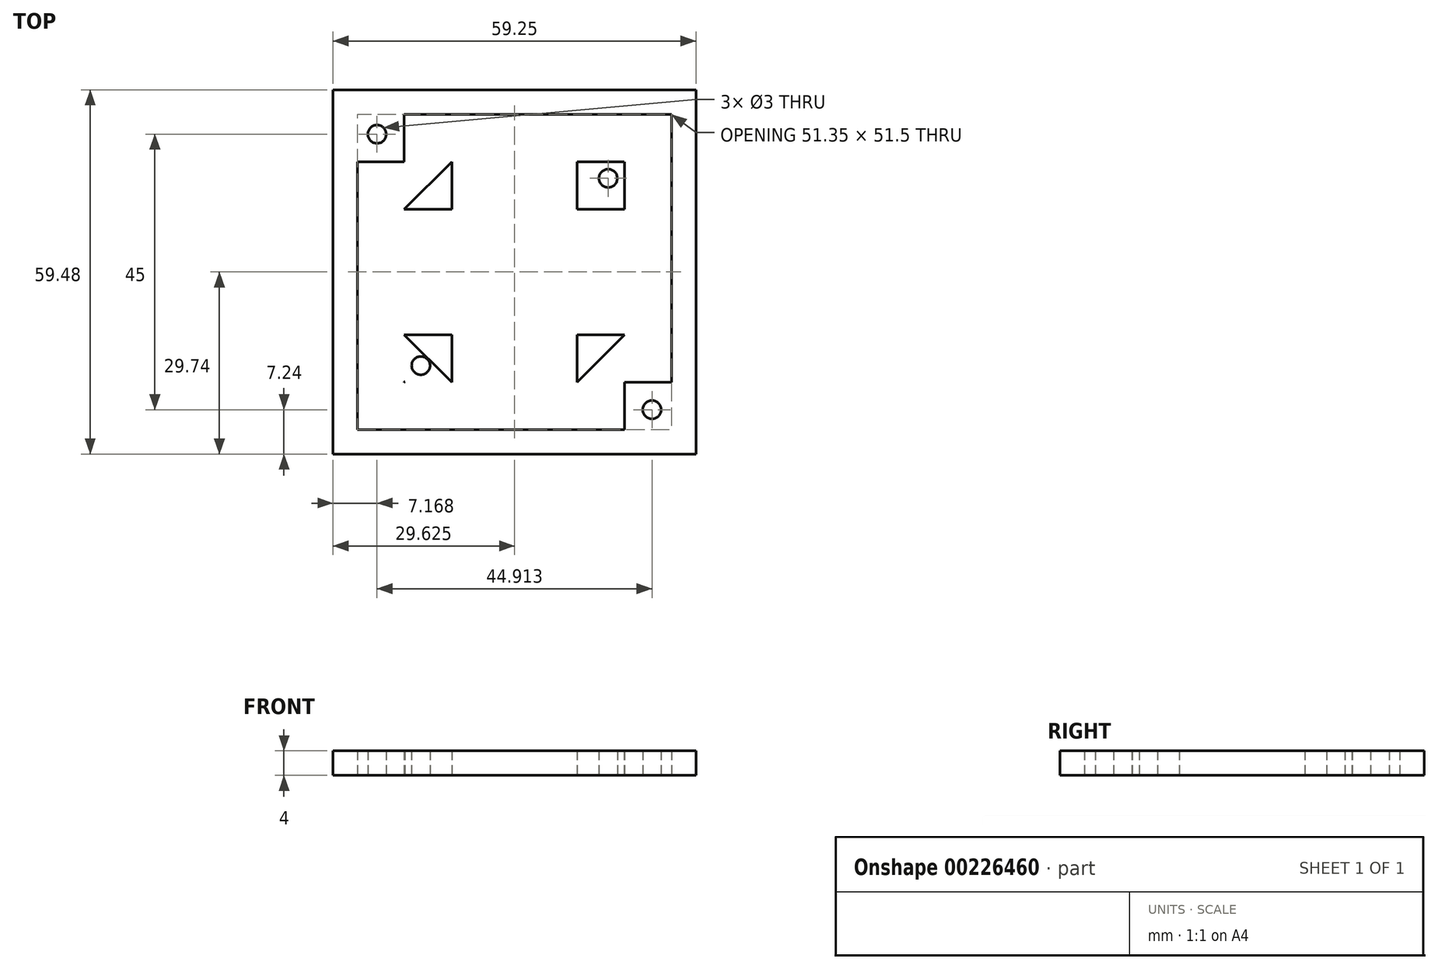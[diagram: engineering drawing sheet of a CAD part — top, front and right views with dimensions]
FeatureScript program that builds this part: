
annotation { "Feature Type Name" : "Feature", "Feature Type Description" : "" }
export const myFeature = defineFeature(function(context is Context, id is Id, definition is map)
    precondition{}
    {
        {
            var Q0;
            Q0=qCreatedBy(makeId("Top.planeOp"),FACE);
            var sketch = newSketch(context, id + "F0", { "sketchPlane" : qUnion([Q0])});
            skLineSegment(sketch, "E0.bottom", {"start": v(0, -51.5) * mm, "end": v(51.35, -51.5) * mm});
            skLineSegment(sketch, "E0.top", {"start": v(0, 0) * mm, "end": v(51.35, 0) * mm});
            skLineSegment(sketch, "E0.left", {"start": v(0, -51.5) * mm, "end": v(0, 0) * mm});
            skLineSegment(sketch, "E0.right", {"start": v(51.35, -51.5) * mm, "end": v(51.35, 0) * mm});
            skLineSegment(sketch, "E1.bottom", {"start": v(7.68, -43.75) * mm, "end": v(43.68, -43.75) * mm});
            skLineSegment(sketch, "E1.top", {"start": v(7.68, -7.75) * mm, "end": v(43.68, -7.75) * mm});
            skLineSegment(sketch, "E1.left", {"start": v(7.67, -43.75) * mm, "end": v(7.67, -7.75) * mm});
            skLineSegment(sketch, "E1.right", {"start": v(43.68, -43.75) * mm, "end": v(43.68, -7.75) * mm});
            skLineSegment(sketch, "E2", {"start": v(7.67, -7.75) * mm, "end": v(0, 0) * mm});
            skLineSegment(sketch, "E3", {"start": v(43.68, -7.75) * mm, "end": v(51.35, 0) * mm});
            skLineSegment(sketch, "E4", {"start": v(43.68, -43.75) * mm, "end": v(51.35, -51.5) * mm});
            skLineSegment(sketch, "E5", {"start": v(7.67, -43.75) * mm, "end": v(0, -51.5) * mm});
            skLineSegment(sketch, "E6.bottom", {"start": v(7.67, -7.75) * mm, "end": v(15.42, -7.75) * mm});
            skLineSegment(sketch, "E6.top", {"start": v(7.68, -15.5) * mm, "end": v(15.42, -15.5) * mm});
            skLineSegment(sketch, "E6.left", {"start": v(7.67, -7.75) * mm, "end": v(7.67, -15.5) * mm});
            skLineSegment(sketch, "E6.right", {"start": v(15.42, -7.75) * mm, "end": v(15.42, -15.5) * mm});
            skLineSegment(sketch, "E7.bottom", {"start": v(43.68, -7.75) * mm, "end": v(35.93, -7.75) * mm});
            skLineSegment(sketch, "E7.top", {"start": v(43.68, -15.5) * mm, "end": v(35.93, -15.5) * mm});
            skLineSegment(sketch, "E7.left", {"start": v(43.68, -7.75) * mm, "end": v(43.68, -15.5) * mm});
            skLineSegment(sketch, "E7.right", {"start": v(35.93, -7.75) * mm, "end": v(35.93, -15.5) * mm});
            skLineSegment(sketch, "E8.bottom", {"start": v(43.68, -43.75) * mm, "end": v(35.93, -43.75) * mm});
            skLineSegment(sketch, "E8.top", {"start": v(43.68, -36) * mm, "end": v(35.93, -36) * mm});
            skLineSegment(sketch, "E8.left", {"start": v(43.68, -43.75) * mm, "end": v(43.68, -36) * mm});
            skLineSegment(sketch, "E8.right", {"start": v(35.93, -43.75) * mm, "end": v(35.93, -36) * mm});
            skLineSegment(sketch, "E9.bottom", {"start": v(7.67, -43.75) * mm, "end": v(15.42, -43.75) * mm});
            skLineSegment(sketch, "E9.top", {"start": v(7.67, -36) * mm, "end": v(15.42, -36) * mm});
            skLineSegment(sketch, "E9.left", {"start": v(7.67, -43.75) * mm, "end": v(7.67, -36) * mm});
            skLineSegment(sketch, "E9.right", {"start": v(15.42, -43.75) * mm, "end": v(15.42, -36) * mm});
            skLineSegment(sketch, "E10", {"start": v(7.67, -7.75) * mm, "end": v(15.42, -15.5) * mm});
            skLineSegment(sketch, "E11", {"start": v(7.68, -15.5) * mm, "end": v(15.43, -7.75) * mm});
            skLineSegment(sketch, "E12", {"start": v(7.67, -43.75) * mm, "end": v(15.42, -36) * mm});
            skLineSegment(sketch, "E13", {"start": v(7.68, -36) * mm, "end": v(15.42, -43.75) * mm});
            skLineSegment(sketch, "E14", {"start": v(25.68, -43.75) * mm, "end": v(25.68, -7.75) * mm});
            skCircle(sketch, "E15", {"center": v(10.37, -10.45) * mm, "radius": 1.5 * mm});
            skLineSegment(sketch, "E16", {"start": v(7.68, -25.75) * mm, "end": v(43.68, -25.75) * mm});
            skLineSegment(sketch, "E17.MirrorCS", {"start": v(43.68, -7.75) * mm, "end": v(35.93, -15.5) * mm});
            skCircle(sketch, "E18.MirrorC", {"center": v(40.98, -10.45) * mm, "radius": 1.5 * mm});
            skLineSegment(sketch, "E19.MirrorCS", {"start": v(43.68, -15.5) * mm, "end": v(35.93, -7.75) * mm});
            skCircle(sketch, "E20.MirrorC", {"center": v(40.98, -41.05) * mm, "radius": 1.5 * mm});
            skLineSegment(sketch, "E21.MirrorCS", {"start": v(43.68, -36) * mm, "end": v(35.93, -43.75) * mm});
            skLineSegment(sketch, "E22.MirrorCS", {"start": v(43.68, -43.75) * mm, "end": v(35.93, -36) * mm});
            skLineSegment(sketch, "E23.MirrorCS", {"start": v(7.67, -36) * mm, "end": v(15.42, -43.75) * mm});
            skCircle(sketch, "E24.MirrorC", {"center": v(10.37, -41.05) * mm, "radius": 1.5 * mm});
            skLineSegment(sketch, "E25.MirrorCS", {"start": v(7.68, -43.75) * mm, "end": v(15.43, -36) * mm});
            skLineSegment(sketch, "E26.bottom", {"start": v(0, 0) * mm, "end": v(7.67, 0) * mm});
            skLineSegment(sketch, "E26.top", {"start": v(0, -7.75) * mm, "end": v(7.67, -7.75) * mm});
            skLineSegment(sketch, "E26.left", {"start": v(0, 0) * mm, "end": v(0, -7.75) * mm});
            skLineSegment(sketch, "E26.right", {"start": v(7.67, 0) * mm, "end": v(7.67, -7.75) * mm});
            skLineSegment(sketch, "E27.bottom", {"start": v(43.6, -7.83) * mm, "end": v(51.35, -7.83) * mm});
            skLineSegment(sketch, "E27.top", {"start": v(43.6, 0) * mm, "end": v(51.35, 0) * mm});
            skLineSegment(sketch, "E27.left", {"start": v(43.6, -7.83) * mm, "end": v(43.6, 0) * mm});
            skLineSegment(sketch, "E27.right", {"start": v(51.35, -7.83) * mm, "end": v(51.35, 0) * mm});
            skLineSegment(sketch, "E28.bottom", {"start": v(51.35, -51.5) * mm, "end": v(43.68, -51.5) * mm});
            skLineSegment(sketch, "E28.top", {"start": v(51.35, -43.75) * mm, "end": v(43.68, -43.75) * mm});
            skLineSegment(sketch, "E28.left", {"start": v(51.35, -51.5) * mm, "end": v(51.35, -43.75) * mm});
            skLineSegment(sketch, "E28.right", {"start": v(43.68, -51.5) * mm, "end": v(43.68, -43.75) * mm});
            skLineSegment(sketch, "E29.bottom", {"start": v(0, -51.5) * mm, "end": v(7.75, -51.5) * mm});
            skLineSegment(sketch, "E29.top", {"start": v(0, -43.67) * mm, "end": v(7.75, -43.67) * mm});
            skLineSegment(sketch, "E29.left", {"start": v(0, -51.5) * mm, "end": v(0, -43.67) * mm});
            skLineSegment(sketch, "E29.right", {"start": v(7.75, -51.5) * mm, "end": v(7.75, -43.67) * mm});
            skCircle(sketch, "E30", {"center": v(3.22, -3.25) * mm, "radius": 1.5 * mm});
            skPoint(sketch, "E30.centerSnap0", {"position": v(3.84, 0) * mm});
            skCircle(sketch, "E31.MirrorC", {"center": v(3.22, -48.25) * mm, "radius": 1.5 * mm});
            skCircle(sketch, "E32.MirrorC", {"center": v(48.13, -3.25) * mm, "radius": 1.5 * mm});
            skCircle(sketch, "E33.MirrorC", {"center": v(48.13, -48.25) * mm, "radius": 1.5 * mm});
            skLineSegment(sketch, "E34", {"start": v(0, 0) * mm, "end": v(-3.95, 3.99) * mm});
            skLineSegment(sketch, "E35", {"start": v(-3.95, 3.99) * mm, "end": v(55.3, 3.99) * mm});
            skLineSegment(sketch, "E36", {"start": v(55.3, 3.99) * mm, "end": v(51.35, 0) * mm});
            skLineSegment(sketch, "E37", {"start": v(55.3, 3.99) * mm, "end": v(55.3, -55.49) * mm});
            skLineSegment(sketch, "E38", {"start": v(55.3, -55.49) * mm, "end": v(51.35, -51.5) * mm});
            skLineSegment(sketch, "E39", {"start": v(55.3, -55.49) * mm, "end": v(-3.95, -55.49) * mm});
            skLineSegment(sketch, "E40", {"start": v(-3.95, -55.49) * mm, "end": v(0, -51.5) * mm});
            skLineSegment(sketch, "E41", {"start": v(-3.95, -55.49) * mm, "end": v(-3.95, 3.99) * mm});
            skSolve(sketch);
        }
        {
            var Q0;
            Q0=makeQuery(id+"F0.imprint","IMPRINT",FACE,{"disambiguationData":[TD([[makeQuery(id+"F0.imprint","IMPRINT",EDGE,{"derivedFrom":sQuery(id+"F0.wireOp",EDGE,"E0.left")}),-1.0]])]});
            var Q1;
            {var subQ0=sQuery(id+"F0.wireOp",EDGE,"E26.top");Q1=makeQuery(id+"F0.imprint","IMPRINT",FACE,{"disambiguationData":[TD([[makeQuery(id+"F0.imprint","IMPRINT",EDGE,{"derivedFrom":subQ0}),1.0]])]});}
            var Q2;
            {var subQ1=sQuery(id+"F0.wireOp",EDGE,"E26.bottom");Q2=makeQuery(id+"F0.imprint","IMPRINT",FACE,{"disambiguationData":[TD([[makeQuery(id+"F0.imprint","IMPRINT",EDGE,{"derivedFrom":subQ1}),-1.0]])]});}
            var Q3;
            Q3=makeQuery(id+"F0.imprint","IMPRINT",FACE,{"disambiguationData":[TD([[makeQuery(id+"F0.imprint","IMPRINT",EDGE,{"derivedFrom":sQuery(id+"F0.wireOp",EDGE,"E0.top")}),-1.0]])]});
            var Q4;
            Q4=makeQuery(id+"F0.imprint","IMPRINT",FACE,{"disambiguationData":[TD([[makeQuery(id+"F0.imprint","IMPRINT",EDGE,{"derivedFrom":sQuery(id+"F0.wireOp",EDGE,"E0.right")}),1.0]])]});
            var Q5;
            {var subQ1=sQuery(id+"F0.wireOp",EDGE,"E27.bottom");Q5=makeQuery(id+"F0.imprint","IMPRINT",FACE,{"disambiguationData":[TD([[makeQuery(id+"F0.imprint","IMPRINT",EDGE,{"derivedFrom":subQ1}),1.0]])]});}
            var Q6;
            {var subQ0=sQuery(id+"F0.wireOp",EDGE,"E27.top");Q6=makeQuery(id+"F0.imprint","IMPRINT",FACE,{"disambiguationData":[TD([[makeQuery(id+"F0.imprint","IMPRINT",EDGE,{"derivedFrom":subQ0}),-1.0]])]});}
            var Q7;
            {var subQ0=sQuery(id+"F0.wireOp",EDGE,"E6.left");Q7=makeQuery(id+"F0.imprint","IMPRINT",FACE,{"disambiguationData":[TD([[makeQuery(id+"F0.imprint","IMPRINT",EDGE,{"derivedFrom":subQ0}),1.0]])]});}
            var Q8;
            {var subQ0=sQuery(id+"F0.wireOp",EDGE,"E6.top");Q8=makeQuery(id+"F0.imprint","IMPRINT",FACE,{"disambiguationData":[TD([[makeQuery(id+"F0.imprint","IMPRINT",EDGE,{"derivedFrom":subQ0}),1.0]])]});}
            var Q9;
            {var subQ0=sQuery(id+"F0.wireOp",EDGE,"E6.right");Q9=makeQuery(id+"F0.imprint","IMPRINT",FACE,{"disambiguationData":[TD([[makeQuery(id+"F0.imprint","IMPRINT",EDGE,{"derivedFrom":subQ0}),-1.0]])]});}
            var Q10;
            {var subQ0=sQuery(id+"F0.wireOp",EDGE,"E6.bottom");Q10=makeQuery(id+"F0.imprint","IMPRINT",FACE,{"disambiguationData":[TD([[makeQuery(id+"F0.imprint","IMPRINT",EDGE,{"derivedFrom":subQ0}),-1.0]])]});}
            var Q11;
            {var subQ0=sQuery(id+"F0.wireOp",EDGE,"E7.left");Q11=makeQuery(id+"F0.imprint","IMPRINT",FACE,{"disambiguationData":[TD([[makeQuery(id+"F0.imprint","IMPRINT",EDGE,{"derivedFrom":subQ0}),-1.0]])]});}
            var Q12;
            {var subQ0=sQuery(id+"F0.wireOp",EDGE,"E7.bottom");Q12=makeQuery(id+"F0.imprint","IMPRINT",FACE,{"disambiguationData":[TD([[makeQuery(id+"F0.imprint","IMPRINT",EDGE,{"derivedFrom":subQ0}),1.0]])]});}
            var Q13;
            {var subQ0=sQuery(id+"F0.wireOp",EDGE,"E8.top");Q13=makeQuery(id+"F0.imprint","IMPRINT",FACE,{"disambiguationData":[TD([[makeQuery(id+"F0.imprint","IMPRINT",EDGE,{"derivedFrom":subQ0}),1.0]])]});}
            var Q14;
            {var subQ0=sQuery(id+"F0.wireOp",EDGE,"E8.right");Q14=makeQuery(id+"F0.imprint","IMPRINT",FACE,{"disambiguationData":[TD([[makeQuery(id+"F0.imprint","IMPRINT",EDGE,{"derivedFrom":subQ0}),-1.0]])]});}
            var Q15;
            {var subQ0=sQuery(id+"F0.wireOp",EDGE,"E8.bottom");Q15=makeQuery(id+"F0.imprint","IMPRINT",FACE,{"disambiguationData":[TD([[makeQuery(id+"F0.imprint","IMPRINT",EDGE,{"derivedFrom":subQ0}),-1.0]])]});}
            var Q16;
            Q16=makeQuery(id+"F0.imprint","IMPRINT",FACE,{"disambiguationData":[TD([[makeQuery(id+"F0.imprint","IMPRINT",EDGE,{"derivedFrom":sQuery(id+"F0.wireOp",EDGE,"E0.bottom")}),1.0]])]});
            var Q17;
            {var subQ0=sQuery(id+"F0.wireOp",EDGE,"E8.left");Q17=makeQuery(id+"F0.imprint","IMPRINT",FACE,{"disambiguationData":[TD([[makeQuery(id+"F0.imprint","IMPRINT",EDGE,{"derivedFrom":subQ0}),1.0]])]});}
            var Q18;
            {var subQ0=sQuery(id+"F0.wireOp",EDGE,"E9.bottom");Q18=makeQuery(id+"F0.imprint","IMPRINT",FACE,{"disambiguationData":[TD([[makeQuery(id+"F0.imprint","IMPRINT",EDGE,{"derivedFrom":subQ0}),1.0]])]});}
            var Q19;
            {var subQ0=sQuery(id+"F0.wireOp",EDGE,"E9.left");Q19=makeQuery(id+"F0.imprint","IMPRINT",FACE,{"disambiguationData":[TD([[makeQuery(id+"F0.imprint","IMPRINT",EDGE,{"derivedFrom":subQ0}),-1.0]])]});}
            var Q20;
            {var subQ0=sQuery(id+"F0.wireOp",EDGE,"E29.top");Q20=makeQuery(id+"F0.imprint","IMPRINT",FACE,{"disambiguationData":[TD([[makeQuery(id+"F0.imprint","IMPRINT",EDGE,{"derivedFrom":subQ0}),-1.0]])]});}
            var Q21;
            {var subQ1=sQuery(id+"F0.wireOp",EDGE,"E29.bottom");Q21=makeQuery(id+"F0.imprint","IMPRINT",FACE,{"disambiguationData":[TD([[makeQuery(id+"F0.imprint","IMPRINT",EDGE,{"derivedFrom":subQ1}),1.0]])]});}
            var Q22;
            {var subQ1=sQuery(id+"F0.wireOp",EDGE,"E28.bottom");Q22=makeQuery(id+"F0.imprint","IMPRINT",FACE,{"disambiguationData":[TD([[makeQuery(id+"F0.imprint","IMPRINT",EDGE,{"derivedFrom":subQ1}),-1.0]])]});}
            var Q23;
            {var subQ0=sQuery(id+"F0.wireOp",EDGE,"E28.top");Q23=makeQuery(id+"F0.imprint","IMPRINT",FACE,{"disambiguationData":[TD([[makeQuery(id+"F0.imprint","IMPRINT",EDGE,{"derivedFrom":subQ0}),1.0]])]});}
            var Q24;
            {var subQ0=sQuery(id+"F0.wireOp",EDGE,"E9.top");Q24=makeQuery(id+"F0.imprint","IMPRINT",FACE,{"disambiguationData":[TD([[makeQuery(id+"F0.imprint","IMPRINT",EDGE,{"derivedFrom":subQ0}),-1.0]])]});}
            var Q25;
            {var subQ0=sQuery(id+"F0.wireOp",EDGE,"E9.right");Q25=makeQuery(id+"F0.imprint","IMPRINT",FACE,{"disambiguationData":[TD([[makeQuery(id+"F0.imprint","IMPRINT",EDGE,{"derivedFrom":subQ0}),1.0]])]});}
            var Q26;
            {var subQ0=sQuery(id+"F0.wireOp",EDGE,"E25.MirrorCS");var subQ1=sQuery(id+"F0.wireOp",EDGE,"E24.MirrorC");var subQ2=makeQuery(id+"F0.imprint","INTERSECT",VERTEX,{"disambiguationData":[OD(0.0)],"derivedFrom":[subQ1,subQ0]});Q26=makeQuery(id+"F0.imprint","IMPRINT",FACE,{"disambiguationData":[TD([[makeQuery(id+"F0.imprint","IMPRINT",EDGE,{"disambiguationData":[TD([[subQ2,1.0]])],"derivedFrom":subQ1}),1.0]])]});}
            var Q27;
            {var subQ0=sQuery(id+"F0.wireOp",EDGE,"E25.MirrorCS");var subQ1=sQuery(id+"F0.wireOp",EDGE,"E24.MirrorC");var subQ2=makeQuery(id+"F0.imprint","INTERSECT",VERTEX,{"disambiguationData":[OD(0.0)],"derivedFrom":[subQ1,subQ0]});Q27=makeQuery(id+"F0.imprint","IMPRINT",FACE,{"disambiguationData":[TD([[makeQuery(id+"F0.imprint","IMPRINT",EDGE,{"disambiguationData":[TD([[subQ2,-1.0]])],"derivedFrom":subQ1}),1.0]])]});}
            var Q28;
            {var subQ0=sQuery(id+"F0.wireOp",EDGE,"E7.right");Q28=makeQuery(id+"F0.imprint","IMPRINT",FACE,{"disambiguationData":[TD([[makeQuery(id+"F0.imprint","IMPRINT",EDGE,{"derivedFrom":subQ0}),1.0]])]});}
            var Q29;
            {var subQ0=sQuery(id+"F0.wireOp",EDGE,"E7.top");Q29=makeQuery(id+"F0.imprint","IMPRINT",FACE,{"disambiguationData":[TD([[makeQuery(id+"F0.imprint","IMPRINT",EDGE,{"derivedFrom":subQ0}),-1.0]])]});}
            var Q30;
            {var subQ1=sQuery(id+"F0.wireOp",EDGE,"E17.MirrorCS");var subQ6=sQuery(id+"F0.wireOp",EDGE,"E27.left");var subQ7=makeQuery(id+"F0.imprint","INTERSECT",VERTEX,{"derivedFrom":[subQ1,subQ6]});Q30=makeQuery(id+"F0.imprint","IMPRINT",FACE,{"disambiguationData":[TD([[makeQuery(id+"F0.imprint","IMPRINT",EDGE,{"disambiguationData":[TD([[subQ7,-1.0]])],"derivedFrom":subQ1}),-1.0]])]});}
            var Q31;
            {var subQ1=sQuery(id+"F0.wireOp",EDGE,"E17.MirrorCS");var subQ6=sQuery(id+"F0.wireOp",EDGE,"E27.left");var subQ7=makeQuery(id+"F0.imprint","INTERSECT",VERTEX,{"derivedFrom":[subQ1,subQ6]});Q31=makeQuery(id+"F0.imprint","IMPRINT",FACE,{"disambiguationData":[TD([[makeQuery(id+"F0.imprint","IMPRINT",EDGE,{"disambiguationData":[TD([[subQ7,-1.0]])],"derivedFrom":subQ1}),1.0]])]});}
            var Q32;
            {var subQ8=sQuery(id+"F0.wireOp",EDGE,"E29.left");Q32=makeQuery(id+"F0.imprint","IMPRINT",FACE,{"disambiguationData":[TD([[makeQuery(id+"F0.imprint","IMPRINT",EDGE,{"derivedFrom":subQ8}),-1.0]])]});}
            var Q33;
            {var subQ8=sQuery(id+"F0.wireOp",EDGE,"E27.right");Q33=makeQuery(id+"F0.imprint","IMPRINT",FACE,{"disambiguationData":[TD([[makeQuery(id+"F0.imprint","IMPRINT",EDGE,{"derivedFrom":subQ8}),1.0]])]});}
            extrude(context, id + "F1", {"entities" : qUnion([Q0, Q1, Q2, Q3, Q4, Q5, Q6, Q7, Q8, Q9, Q10, Q11, Q12, Q13, Q14, Q15, Q16, Q17, Q18, Q19, Q20, Q21, Q22, Q23, Q24, Q25, Q26, Q27, Q28, Q29, Q30, Q31, Q32, Q33]), "depth" : 2 * mm});
        }
        {
            var Q0;
            {var subQ1=sQuery(id+"F0.wireOp",EDGE,"E29.bottom");Q0=makeQuery(id+"F0.imprint","IMPRINT",FACE,{"disambiguationData":[TD([[makeQuery(id+"F0.imprint","IMPRINT",EDGE,{"derivedFrom":subQ1}),1.0]])]});}
            var Q1;
            {var subQ0=sQuery(id+"F0.wireOp",EDGE,"E29.top");Q1=makeQuery(id+"F0.imprint","IMPRINT",FACE,{"disambiguationData":[TD([[makeQuery(id+"F0.imprint","IMPRINT",EDGE,{"derivedFrom":subQ0}),-1.0]])]});}
            var Q2;
            {var subQ0=sQuery(id+"F0.wireOp",EDGE,"E27.top");Q2=makeQuery(id+"F0.imprint","IMPRINT",FACE,{"disambiguationData":[TD([[makeQuery(id+"F0.imprint","IMPRINT",EDGE,{"derivedFrom":subQ0}),-1.0]])]});}
            var Q3;
            {var subQ1=sQuery(id+"F0.wireOp",EDGE,"E27.bottom");Q3=makeQuery(id+"F0.imprint","IMPRINT",FACE,{"disambiguationData":[TD([[makeQuery(id+"F0.imprint","IMPRINT",EDGE,{"derivedFrom":subQ1}),1.0]])]});}
            var Q4;
            {var subQ0=sQuery(id+"F0.wireOp",EDGE,"E28.top");Q4=makeQuery(id+"F0.imprint","IMPRINT",FACE,{"disambiguationData":[TD([[makeQuery(id+"F0.imprint","IMPRINT",EDGE,{"derivedFrom":subQ0}),1.0]])]});}
            var Q5;
            {var subQ1=sQuery(id+"F0.wireOp",EDGE,"E28.bottom");Q5=makeQuery(id+"F0.imprint","IMPRINT",FACE,{"disambiguationData":[TD([[makeQuery(id+"F0.imprint","IMPRINT",EDGE,{"derivedFrom":subQ1}),-1.0]])]});}
            var Q6;
            {var subQ0=sQuery(id+"F0.wireOp",EDGE,"E9.right");Q6=makeQuery(id+"F0.imprint","IMPRINT",FACE,{"disambiguationData":[TD([[makeQuery(id+"F0.imprint","IMPRINT",EDGE,{"derivedFrom":subQ0}),1.0]])]});}
            var Q7;
            {var subQ0=sQuery(id+"F0.wireOp",EDGE,"E9.bottom");Q7=makeQuery(id+"F0.imprint","IMPRINT",FACE,{"disambiguationData":[TD([[makeQuery(id+"F0.imprint","IMPRINT",EDGE,{"derivedFrom":subQ0}),1.0]])]});}
            var Q8;
            {var subQ0=sQuery(id+"F0.wireOp",EDGE,"E9.left");Q8=makeQuery(id+"F0.imprint","IMPRINT",FACE,{"disambiguationData":[TD([[makeQuery(id+"F0.imprint","IMPRINT",EDGE,{"derivedFrom":subQ0}),-1.0]])]});}
            var Q9;
            {var subQ0=sQuery(id+"F0.wireOp",EDGE,"E9.top");Q9=makeQuery(id+"F0.imprint","IMPRINT",FACE,{"disambiguationData":[TD([[makeQuery(id+"F0.imprint","IMPRINT",EDGE,{"derivedFrom":subQ0}),-1.0]])]});}
            var Q10;
            {var subQ0=sQuery(id+"F0.wireOp",EDGE,"E8.top");Q10=makeQuery(id+"F0.imprint","IMPRINT",FACE,{"disambiguationData":[TD([[makeQuery(id+"F0.imprint","IMPRINT",EDGE,{"derivedFrom":subQ0}),1.0]])]});}
            var Q11;
            {var subQ0=sQuery(id+"F0.wireOp",EDGE,"E8.left");Q11=makeQuery(id+"F0.imprint","IMPRINT",FACE,{"disambiguationData":[TD([[makeQuery(id+"F0.imprint","IMPRINT",EDGE,{"derivedFrom":subQ0}),1.0]])]});}
            var Q12;
            {var subQ0=sQuery(id+"F0.wireOp",EDGE,"E8.bottom");Q12=makeQuery(id+"F0.imprint","IMPRINT",FACE,{"disambiguationData":[TD([[makeQuery(id+"F0.imprint","IMPRINT",EDGE,{"derivedFrom":subQ0}),-1.0]])]});}
            var Q13;
            {var subQ0=sQuery(id+"F0.wireOp",EDGE,"E8.right");Q13=makeQuery(id+"F0.imprint","IMPRINT",FACE,{"disambiguationData":[TD([[makeQuery(id+"F0.imprint","IMPRINT",EDGE,{"derivedFrom":subQ0}),-1.0]])]});}
            var Q14;
            {var subQ0=sQuery(id+"F0.wireOp",EDGE,"E7.bottom");Q14=makeQuery(id+"F0.imprint","IMPRINT",FACE,{"disambiguationData":[TD([[makeQuery(id+"F0.imprint","IMPRINT",EDGE,{"derivedFrom":subQ0}),1.0]])]});}
            var Q15;
            {var subQ0=sQuery(id+"F0.wireOp",EDGE,"E7.left");Q15=makeQuery(id+"F0.imprint","IMPRINT",FACE,{"disambiguationData":[TD([[makeQuery(id+"F0.imprint","IMPRINT",EDGE,{"derivedFrom":subQ0}),-1.0]])]});}
            var Q16;
            {var subQ0=sQuery(id+"F0.wireOp",EDGE,"E7.top");Q16=makeQuery(id+"F0.imprint","IMPRINT",FACE,{"disambiguationData":[TD([[makeQuery(id+"F0.imprint","IMPRINT",EDGE,{"derivedFrom":subQ0}),-1.0]])]});}
            var Q17;
            {var subQ0=sQuery(id+"F0.wireOp",EDGE,"E7.right");Q17=makeQuery(id+"F0.imprint","IMPRINT",FACE,{"disambiguationData":[TD([[makeQuery(id+"F0.imprint","IMPRINT",EDGE,{"derivedFrom":subQ0}),1.0]])]});}
            var Q18;
            {var subQ0=sQuery(id+"F0.wireOp",EDGE,"E6.right");Q18=makeQuery(id+"F0.imprint","IMPRINT",FACE,{"disambiguationData":[TD([[makeQuery(id+"F0.imprint","IMPRINT",EDGE,{"derivedFrom":subQ0}),-1.0]])]});}
            var Q19;
            {var subQ0=sQuery(id+"F0.wireOp",EDGE,"E6.bottom");Q19=makeQuery(id+"F0.imprint","IMPRINT",FACE,{"disambiguationData":[TD([[makeQuery(id+"F0.imprint","IMPRINT",EDGE,{"derivedFrom":subQ0}),-1.0]])]});}
            var Q20;
            {var subQ0=sQuery(id+"F0.wireOp",EDGE,"E6.top");Q20=makeQuery(id+"F0.imprint","IMPRINT",FACE,{"disambiguationData":[TD([[makeQuery(id+"F0.imprint","IMPRINT",EDGE,{"derivedFrom":subQ0}),1.0]])]});}
            var Q21;
            {var subQ0=sQuery(id+"F0.wireOp",EDGE,"E6.left");Q21=makeQuery(id+"F0.imprint","IMPRINT",FACE,{"disambiguationData":[TD([[makeQuery(id+"F0.imprint","IMPRINT",EDGE,{"derivedFrom":subQ0}),1.0]])]});}
            var Q22;
            {var subQ1=sQuery(id+"F0.wireOp",EDGE,"E26.bottom");Q22=makeQuery(id+"F0.imprint","IMPRINT",FACE,{"disambiguationData":[TD([[makeQuery(id+"F0.imprint","IMPRINT",EDGE,{"derivedFrom":subQ1}),-1.0]])]});}
            var Q23;
            {var subQ0=sQuery(id+"F0.wireOp",EDGE,"E26.top");Q23=makeQuery(id+"F0.imprint","IMPRINT",FACE,{"disambiguationData":[TD([[makeQuery(id+"F0.imprint","IMPRINT",EDGE,{"derivedFrom":subQ0}),1.0]])]});}
            var Q24;
            Q24=makeQuery(id+"F0.imprint","IMPRINT",FACE,{"disambiguationData":[TD([[makeQuery(id+"F0.imprint","IMPRINT",EDGE,{"derivedFrom":sQuery(id+"F0.wireOp",EDGE,"E0.top")}),-1.0]])]});
            var Q25;
            Q25=makeQuery(id+"F0.imprint","IMPRINT",FACE,{"disambiguationData":[TD([[makeQuery(id+"F0.imprint","IMPRINT",EDGE,{"derivedFrom":sQuery(id+"F0.wireOp",EDGE,"E0.right")}),1.0]])]});
            var Q26;
            Q26=makeQuery(id+"F0.imprint","IMPRINT",FACE,{"disambiguationData":[TD([[makeQuery(id+"F0.imprint","IMPRINT",EDGE,{"derivedFrom":sQuery(id+"F0.wireOp",EDGE,"E0.left")}),-1.0]])]});
            var Q27;
            Q27=makeQuery(id+"F0.imprint","IMPRINT",FACE,{"disambiguationData":[TD([[makeQuery(id+"F0.imprint","IMPRINT",EDGE,{"derivedFrom":sQuery(id+"F0.wireOp",EDGE,"E0.bottom")}),1.0]])]});
            var Q28;
            Q28=makeQuery(id+"F0.imprint","IMPRINT",FACE,{"disambiguationData":[TD([[makeQuery(id+"F0.imprint","IMPRINT",EDGE,{"derivedFrom":sQuery(id+"F0.wireOp",EDGE,"E0.left")}),1.0]])]});
            var Q29;
            Q29=makeQuery(id+"F0.imprint","IMPRINT",FACE,{"disambiguationData":[TD([[makeQuery(id+"F0.imprint","IMPRINT",EDGE,{"derivedFrom":sQuery(id+"F0.wireOp",EDGE,"E0.top")}),1.0]])]});
            var Q30;
            Q30=makeQuery(id+"F0.imprint","IMPRINT",FACE,{"disambiguationData":[TD([[makeQuery(id+"F0.imprint","IMPRINT",EDGE,{"derivedFrom":sQuery(id+"F0.wireOp",EDGE,"E0.right")}),-1.0]])]});
            var Q31;
            Q31=makeQuery(id+"F0.imprint","IMPRINT",FACE,{"disambiguationData":[TD([[makeQuery(id+"F0.imprint","IMPRINT",EDGE,{"derivedFrom":sQuery(id+"F0.wireOp",EDGE,"E0.bottom")}),-1.0]])]});
            var Q32;
            {var subQ8=sQuery(id+"F0.wireOp",EDGE,"E29.left");Q32=makeQuery(id+"F0.imprint","IMPRINT",FACE,{"disambiguationData":[TD([[makeQuery(id+"F0.imprint","IMPRINT",EDGE,{"derivedFrom":subQ8}),-1.0]])]});}
            var Q33;
            {var subQ8=sQuery(id+"F0.wireOp",EDGE,"E27.right");Q33=makeQuery(id+"F0.imprint","IMPRINT",FACE,{"disambiguationData":[TD([[makeQuery(id+"F0.imprint","IMPRINT",EDGE,{"derivedFrom":subQ8}),1.0]])]});}
            var Q34;
            {var subQ1=sQuery(id+"F0.wireOp",EDGE,"E17.MirrorCS");var subQ6=sQuery(id+"F0.wireOp",EDGE,"E27.left");var subQ7=makeQuery(id+"F0.imprint","INTERSECT",VERTEX,{"derivedFrom":[subQ1,subQ6]});Q34=makeQuery(id+"F0.imprint","IMPRINT",FACE,{"disambiguationData":[TD([[makeQuery(id+"F0.imprint","IMPRINT",EDGE,{"disambiguationData":[TD([[subQ7,-1.0]])],"derivedFrom":subQ1}),-1.0]])]});}
            var Q35;
            {var subQ1=sQuery(id+"F0.wireOp",EDGE,"E17.MirrorCS");var subQ6=sQuery(id+"F0.wireOp",EDGE,"E27.left");var subQ7=makeQuery(id+"F0.imprint","INTERSECT",VERTEX,{"derivedFrom":[subQ1,subQ6]});Q35=makeQuery(id+"F0.imprint","IMPRINT",FACE,{"disambiguationData":[TD([[makeQuery(id+"F0.imprint","IMPRINT",EDGE,{"disambiguationData":[TD([[subQ7,-1.0]])],"derivedFrom":subQ1}),1.0]])]});}
            var Q36;
            {var subQ0=sQuery(id+"F0.wireOp",EDGE,"E25.MirrorCS");var subQ1=sQuery(id+"F0.wireOp",EDGE,"E24.MirrorC");var subQ2=makeQuery(id+"F0.imprint","INTERSECT",VERTEX,{"disambiguationData":[OD(0.0)],"derivedFrom":[subQ1,subQ0]});Q36=makeQuery(id+"F0.imprint","IMPRINT",FACE,{"disambiguationData":[TD([[makeQuery(id+"F0.imprint","IMPRINT",EDGE,{"disambiguationData":[TD([[subQ2,-1.0]])],"derivedFrom":subQ1}),1.0]])]});}
            var Q37;
            {var subQ0=sQuery(id+"F0.wireOp",EDGE,"E25.MirrorCS");var subQ1=sQuery(id+"F0.wireOp",EDGE,"E24.MirrorC");var subQ2=makeQuery(id+"F0.imprint","INTERSECT",VERTEX,{"disambiguationData":[OD(0.0)],"derivedFrom":[subQ1,subQ0]});Q37=makeQuery(id+"F0.imprint","IMPRINT",FACE,{"disambiguationData":[TD([[makeQuery(id+"F0.imprint","IMPRINT",EDGE,{"disambiguationData":[TD([[subQ2,1.0]])],"derivedFrom":subQ1}),1.0]])]});}
            extrude(context, id + "F2", {"entities" : qUnion([Q0, Q1, Q2, Q3, Q4, Q5, Q6, Q7, Q8, Q9, Q10, Q11, Q12, Q13, Q14, Q15, Q16, Q17, Q18, Q19, Q20, Q21, Q22, Q23, Q24, Q25, Q26, Q27, Q28, Q29, Q30, Q31, Q32, Q33, Q34, Q35, Q36, Q37]), "operationType" : NewBodyOperationType.ADD, "depth" : 4 * mm});
        }
    });
